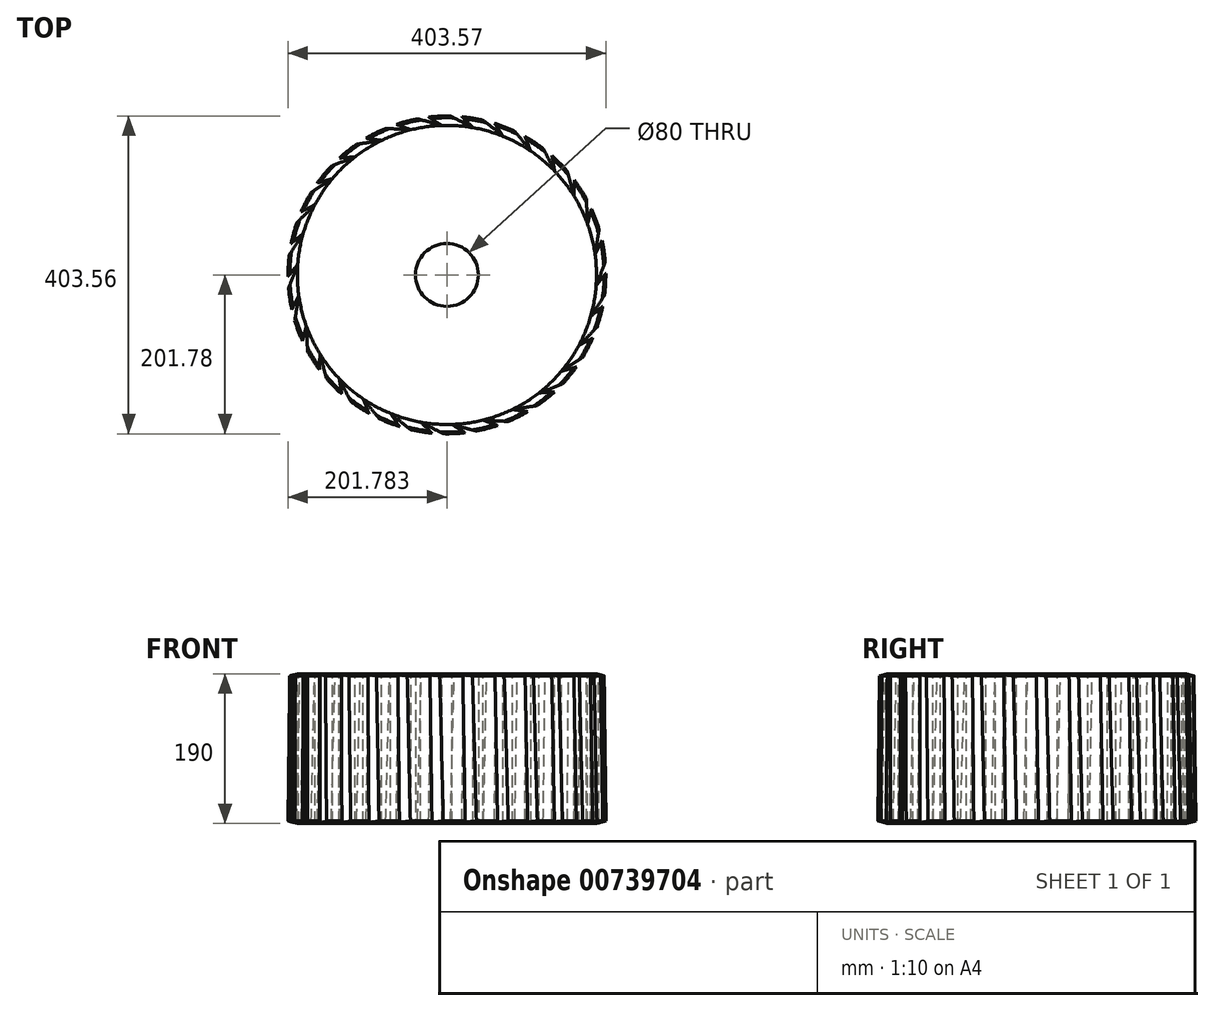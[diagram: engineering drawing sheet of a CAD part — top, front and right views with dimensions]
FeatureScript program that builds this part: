
annotation { "Feature Type Name" : "Feature", "Feature Type Description" : "" }
export const myFeature = defineFeature(function(context is Context, id is Id, definition is map)
    precondition{}
    {
        {
            var Q0;
            Q0=qCreatedBy(makeId("Front.planeOp"),FACE);
            var sketch = newSketch(context, id + "F0", { "sketchPlane" : qUnion([Q0])});
            skLineSegment(sketch, "E0", {"start": v(-135.33, -124.18) * mm, "end": v(-135.33, 192.83) * mm, "construction": true});
            skLineSegment(sketch, "E1.bottom", {"start": v(-325.33, 114.13) * mm, "end": v(-175.33, 114.13) * mm});
            skLineSegment(sketch, "E1.top", {"start": v(-325.33, -75.87) * mm, "end": v(-175.33, -75.87) * mm});
            skLineSegment(sketch, "E1.right", {"start": v(-175.33, 114.13) * mm, "end": v(-175.33, -75.87) * mm});
            skLineSegment(sketch, "E2.right", {"start": v(-334.99, 111.54) * mm, "end": v(-337.11, -72.71) * mm});
            skLineSegment(sketch, "E3", {"start": v(-325.33, 114.13) * mm, "end": v(-334.99, 111.54) * mm});
            skLineSegment(sketch, "E4", {"start": v(-325.33, -75.87) * mm, "end": v(-337.11, -72.71) * mm});
            skSolve(sketch);
        }
        {
            var Q0;
            Q0 = qSketchRegion(id + "F0", true);
            var Q1;
            Q1=sQuery(id+"F0.wireOp",EDGE,"E0");
            revolve(context, id + "F1", {"surfaceOperationType" : NewSurfaceOperationType.NEW, "entities" : qUnion([Q0]), "axis" : qUnion([Q1]), "revolveType" : RevolveType.FULL});
        }
        {
            var Q0;
            Q0=makeQuery(id+"F1.opRevolve","SWEPT_FACE",FACE,{"disambiguationData":[OSD([sQuery(id+"F0.wireOp",EDGE,"E1.bottom")])]});
            var sketch = newSketch(context, id + "F2", { "sketchPlane" : qUnion([Q0])});
            skLineSegment(sketch, "E5", {"start": v(-299.15, 0) * mm, "end": v(273.69, 0) * mm, "construction": true});
            skLineSegment(sketch, "E6", {"start": v(1.56, 131.77) * mm, "end": v(-33.5, 200.96) * mm});
            skLineSegment(sketch, "E7", {"start": v(1.56, 131.77) * mm, "end": v(-10.46, 200.96) * mm});
            skLineSegment(sketch, "E8", {"start": v(-33.5, 200.96) * mm, "end": v(-10.46, 200.96) * mm});
            skPoint(sketch, "E9.end.orphan", {"position": v(-68.57, 270.16) * mm});
            skSolve(sketch);
        }
        {
            var Q0;
            Q0=makeQuery(id+"F2.imprint","IMPRINT",FACE,{"disambiguationData":[TD([[makeQuery(id+"F2.imprint","IMPRINT",EDGE,{"derivedFrom":sQuery(id+"F2.wireOp",EDGE,"E6")}),-1.0]])]});
            extrude(context, id + "F3", {"entities" : qUnion([Q0]), "depth" : 25 * mm, "offsetDistance" : 25 * mm});
        }
        {
            var Q0;
            Q0=makeQuery(id+"F3.opExtrude","CAP_FACE",FACE,{"disambiguationData":[OSD([sQuery(id+"F2.wireOp",EDGE,"E6"),sQuery(id+"F2.wireOp",EDGE,"E7"),sQuery(id+"F2.wireOp",EDGE,"E8")])],"isStart":false});
            extrude(context, id + "F4", {"entities" : qUnion([Q0]), "oppositeDirection" : true, "depth" : 533 * mm, "offsetDistance" : 25 * mm});
        }
        {
            var Q0;
            Q0=makeQuery(id+"F4.opExtrude","SWEPT_BODY",BODY,{"disambiguationData":[OSD([sQuery(id+"F2.wireOp",EDGE,"E6"),sQuery(id+"F2.wireOp",EDGE,"E7"),sQuery(id+"F2.wireOp",EDGE,"E8")])]});
            var Q1;
            Q1=makeQuery(id+"F1.opRevolve","SWEPT_EDGE",EDGE,{"disambiguationData":[OSD([sQuery(id+"F0.wireOp",EDGE,"E1.bottom"),sQuery(id+"F0.wireOp",EDGE,"E1.right")])]});
            circularPattern(context, id + "F5", {"entities" : qUnion([Q0]), "axis" : qUnion([Q1]), "angle" : 360 * degree, "instanceCount" : 30, "equalSpace" : true});
        }
        {
            var Q0;
            Q0=makeQuery(id+"F4.opExtrude","SWEPT_BODY",BODY,{"disambiguationData":[OSD([sQuery(id+"F2.wireOp",EDGE,"E6"),sQuery(id+"F2.wireOp",EDGE,"E7"),sQuery(id+"F2.wireOp",EDGE,"E8")])]});
            var Q1;
            Q1=makeQuery(id+"F5.opPattern","COPY",BODY,{"derivedFrom":makeQuery(id+"F4.opExtrude","SWEPT_BODY",BODY,{"disambiguationData":[OSD([sQuery(id+"F2.wireOp",EDGE,"E6"),sQuery(id+"F2.wireOp",EDGE,"E7"),sQuery(id+"F2.wireOp",EDGE,"E8")])]}),"instanceName":"25"});
            var Q2;
            Q2=makeQuery(id+"F1.opRevolve","SWEPT_BODY",BODY,{"disambiguationData":[OSD([sQuery(id+"F0.wireOp",EDGE,"E1.bottom"),sQuery(id+"F0.wireOp",EDGE,"E1.top"),sQuery(id+"F0.wireOp",EDGE,"E1.right"),sQuery(id+"F0.wireOp",EDGE,"E2.right"),sQuery(id+"F0.wireOp",EDGE,"E3"),sQuery(id+"F0.wireOp",EDGE,"bRj0GN2x-NEWe-g299-EKp4-hdbKCvh0yDdA")])]});
            booleanBodies(context, id + "F6", {"operationType" : BooleanOperationType.SUBTRACTION, "tools" : qUnion([Q0, Q1]), "targets" : qUnion([Q2])});
        }
        {
            var Q0;
            Q0=makeQuery(id+"F3.opExtrude","SWEPT_BODY",BODY,{"disambiguationData":[OSD([sQuery(id+"F2.wireOp",EDGE,"E6"),sQuery(id+"F2.wireOp",EDGE,"E7"),sQuery(id+"F2.wireOp",EDGE,"E8")])]});
            var Q1;
            Q1=makeQuery(id+"F5.opPattern","COPY",BODY,{"derivedFrom":makeQuery(id+"F4.opExtrude","SWEPT_BODY",BODY,{"disambiguationData":[OSD([sQuery(id+"F2.wireOp",EDGE,"E6"),sQuery(id+"F2.wireOp",EDGE,"E7"),sQuery(id+"F2.wireOp",EDGE,"E8")])]}),"instanceName":"1"});
            var Q2;
            Q2=makeQuery(id+"F5.opPattern","COPY",BODY,{"derivedFrom":makeQuery(id+"F4.opExtrude","SWEPT_BODY",BODY,{"disambiguationData":[OSD([sQuery(id+"F2.wireOp",EDGE,"E6"),sQuery(id+"F2.wireOp",EDGE,"E7"),sQuery(id+"F2.wireOp",EDGE,"E8")])]}),"instanceName":"2"});
            var Q3;
            Q3=makeQuery(id+"F1.opRevolve","SWEPT_BODY",BODY,{"disambiguationData":[OSD([sQuery(id+"F0.wireOp",EDGE,"E1.bottom"),sQuery(id+"F0.wireOp",EDGE,"E1.top"),sQuery(id+"F0.wireOp",EDGE,"E1.right"),sQuery(id+"F0.wireOp",EDGE,"E2.right"),sQuery(id+"F0.wireOp",EDGE,"E3"),sQuery(id+"F0.wireOp",EDGE,"bRj0GN2x-NEWe-g299-EKp4-hdbKCvh0yDdA")])]});
            booleanBodies(context, id + "F7", {"operationType" : BooleanOperationType.SUBTRACTION, "tools" : qUnion([Q0, Q1, Q2]), "targets" : qUnion([Q3])});
        }
        {
            var Q0;
            Q0=makeQuery(id+"F5.opPattern","COPY",BODY,{"derivedFrom":makeQuery(id+"F4.opExtrude","SWEPT_BODY",BODY,{"disambiguationData":[OSD([sQuery(id+"F2.wireOp",EDGE,"E6"),sQuery(id+"F2.wireOp",EDGE,"E7"),sQuery(id+"F2.wireOp",EDGE,"E8")])]}),"instanceName":"24"});
            var Q1;
            Q1=makeQuery(id+"F5.opPattern","COPY",BODY,{"derivedFrom":makeQuery(id+"F4.opExtrude","SWEPT_BODY",BODY,{"disambiguationData":[OSD([sQuery(id+"F2.wireOp",EDGE,"E6"),sQuery(id+"F2.wireOp",EDGE,"E7"),sQuery(id+"F2.wireOp",EDGE,"E8")])]}),"instanceName":"23"});
            var Q2;
            Q2=makeQuery(id+"F5.opPattern","COPY",BODY,{"derivedFrom":makeQuery(id+"F4.opExtrude","SWEPT_BODY",BODY,{"disambiguationData":[OSD([sQuery(id+"F2.wireOp",EDGE,"E6"),sQuery(id+"F2.wireOp",EDGE,"E7"),sQuery(id+"F2.wireOp",EDGE,"E8")])]}),"instanceName":"22"});
            var Q3;
            Q3=makeQuery(id+"F5.opPattern","COPY",BODY,{"derivedFrom":makeQuery(id+"F4.opExtrude","SWEPT_BODY",BODY,{"disambiguationData":[OSD([sQuery(id+"F2.wireOp",EDGE,"E6"),sQuery(id+"F2.wireOp",EDGE,"E7"),sQuery(id+"F2.wireOp",EDGE,"E8")])]}),"instanceName":"21"});
            var Q4;
            Q4=makeQuery(id+"F5.opPattern","COPY",BODY,{"derivedFrom":makeQuery(id+"F4.opExtrude","SWEPT_BODY",BODY,{"disambiguationData":[OSD([sQuery(id+"F2.wireOp",EDGE,"E6"),sQuery(id+"F2.wireOp",EDGE,"E7"),sQuery(id+"F2.wireOp",EDGE,"E8")])]}),"instanceName":"20"});
            var Q5;
            Q5=makeQuery(id+"F1.opRevolve","SWEPT_BODY",BODY,{"disambiguationData":[OSD([sQuery(id+"F0.wireOp",EDGE,"E1.bottom"),sQuery(id+"F0.wireOp",EDGE,"E1.top"),sQuery(id+"F0.wireOp",EDGE,"E1.right"),sQuery(id+"F0.wireOp",EDGE,"E2.right"),sQuery(id+"F0.wireOp",EDGE,"E3"),sQuery(id+"F0.wireOp",EDGE,"bRj0GN2x-NEWe-g299-EKp4-hdbKCvh0yDdA")])]});
            booleanBodies(context, id + "F8", {"operationType" : BooleanOperationType.SUBTRACTION, "tools" : qUnion([Q0, Q1, Q2, Q3, Q4]), "targets" : qUnion([Q5])});
        }
        {
            var Q0;
            Q0=makeQuery(id+"F5.opPattern","COPY",BODY,{"derivedFrom":makeQuery(id+"F4.opExtrude","SWEPT_BODY",BODY,{"disambiguationData":[OSD([sQuery(id+"F2.wireOp",EDGE,"E6"),sQuery(id+"F2.wireOp",EDGE,"E7"),sQuery(id+"F2.wireOp",EDGE,"E8")])]}),"instanceName":"15"});
            var Q1;
            Q1=makeQuery(id+"F5.opPattern","COPY",BODY,{"derivedFrom":makeQuery(id+"F4.opExtrude","SWEPT_BODY",BODY,{"disambiguationData":[OSD([sQuery(id+"F2.wireOp",EDGE,"E6"),sQuery(id+"F2.wireOp",EDGE,"E7"),sQuery(id+"F2.wireOp",EDGE,"E8")])]}),"instanceName":"16"});
            var Q2;
            Q2=makeQuery(id+"F5.opPattern","COPY",BODY,{"derivedFrom":makeQuery(id+"F4.opExtrude","SWEPT_BODY",BODY,{"disambiguationData":[OSD([sQuery(id+"F2.wireOp",EDGE,"E6"),sQuery(id+"F2.wireOp",EDGE,"E7"),sQuery(id+"F2.wireOp",EDGE,"E8")])]}),"instanceName":"17"});
            var Q3;
            Q3=makeQuery(id+"F5.opPattern","COPY",BODY,{"derivedFrom":makeQuery(id+"F4.opExtrude","SWEPT_BODY",BODY,{"disambiguationData":[OSD([sQuery(id+"F2.wireOp",EDGE,"E6"),sQuery(id+"F2.wireOp",EDGE,"E7"),sQuery(id+"F2.wireOp",EDGE,"E8")])]}),"instanceName":"18"});
            var Q4;
            Q4=makeQuery(id+"F5.opPattern","COPY",BODY,{"derivedFrom":makeQuery(id+"F4.opExtrude","SWEPT_BODY",BODY,{"disambiguationData":[OSD([sQuery(id+"F2.wireOp",EDGE,"E6"),sQuery(id+"F2.wireOp",EDGE,"E7"),sQuery(id+"F2.wireOp",EDGE,"E8")])]}),"instanceName":"19"});
            var Q5;
            Q5=makeQuery(id+"F1.opRevolve","SWEPT_BODY",BODY,{"disambiguationData":[OSD([sQuery(id+"F0.wireOp",EDGE,"E1.bottom"),sQuery(id+"F0.wireOp",EDGE,"E1.top"),sQuery(id+"F0.wireOp",EDGE,"E1.right"),sQuery(id+"F0.wireOp",EDGE,"E2.right"),sQuery(id+"F0.wireOp",EDGE,"E3"),sQuery(id+"F0.wireOp",EDGE,"bRj0GN2x-NEWe-g299-EKp4-hdbKCvh0yDdA")])]});
            booleanBodies(context, id + "F9", {"operationType" : BooleanOperationType.SUBTRACTION, "tools" : qUnion([Q0, Q1, Q2, Q3, Q4]), "targets" : qUnion([Q5])});
        }
        {
            var Q0;
            Q0=makeQuery(id+"F5.opPattern","COPY",BODY,{"derivedFrom":makeQuery(id+"F4.opExtrude","SWEPT_BODY",BODY,{"disambiguationData":[OSD([sQuery(id+"F2.wireOp",EDGE,"E6"),sQuery(id+"F2.wireOp",EDGE,"E7"),sQuery(id+"F2.wireOp",EDGE,"E8")])]}),"instanceName":"3"});
            var Q1;
            Q1=makeQuery(id+"F5.opPattern","COPY",BODY,{"derivedFrom":makeQuery(id+"F4.opExtrude","SWEPT_BODY",BODY,{"disambiguationData":[OSD([sQuery(id+"F2.wireOp",EDGE,"E6"),sQuery(id+"F2.wireOp",EDGE,"E7"),sQuery(id+"F2.wireOp",EDGE,"E8")])]}),"instanceName":"4"});
            var Q2;
            Q2=makeQuery(id+"F5.opPattern","COPY",BODY,{"derivedFrom":makeQuery(id+"F4.opExtrude","SWEPT_BODY",BODY,{"disambiguationData":[OSD([sQuery(id+"F2.wireOp",EDGE,"E6"),sQuery(id+"F2.wireOp",EDGE,"E7"),sQuery(id+"F2.wireOp",EDGE,"E8")])]}),"instanceName":"5"});
            var Q3;
            Q3=makeQuery(id+"F5.opPattern","COPY",BODY,{"derivedFrom":makeQuery(id+"F4.opExtrude","SWEPT_BODY",BODY,{"disambiguationData":[OSD([sQuery(id+"F2.wireOp",EDGE,"E6"),sQuery(id+"F2.wireOp",EDGE,"E7"),sQuery(id+"F2.wireOp",EDGE,"E8")])]}),"instanceName":"7"});
            var Q4;
            Q4=makeQuery(id+"F5.opPattern","COPY",BODY,{"derivedFrom":makeQuery(id+"F4.opExtrude","SWEPT_BODY",BODY,{"disambiguationData":[OSD([sQuery(id+"F2.wireOp",EDGE,"E6"),sQuery(id+"F2.wireOp",EDGE,"E7"),sQuery(id+"F2.wireOp",EDGE,"E8")])]}),"instanceName":"6"});
            var Q5;
            Q5=makeQuery(id+"F1.opRevolve","SWEPT_BODY",BODY,{"disambiguationData":[OSD([sQuery(id+"F0.wireOp",EDGE,"E1.bottom"),sQuery(id+"F0.wireOp",EDGE,"E1.top"),sQuery(id+"F0.wireOp",EDGE,"E1.right"),sQuery(id+"F0.wireOp",EDGE,"E2.right"),sQuery(id+"F0.wireOp",EDGE,"E3"),sQuery(id+"F0.wireOp",EDGE,"bRj0GN2x-NEWe-g299-EKp4-hdbKCvh0yDdA")])]});
            booleanBodies(context, id + "F10", {"operationType" : BooleanOperationType.SUBTRACTION, "tools" : qUnion([Q0, Q1, Q2, Q3, Q4]), "targets" : qUnion([Q5])});
        }
        {
            var Q0;
            Q0=makeQuery(id+"F5.opPattern","COPY",BODY,{"derivedFrom":makeQuery(id+"F4.opExtrude","SWEPT_BODY",BODY,{"disambiguationData":[OSD([sQuery(id+"F2.wireOp",EDGE,"E6"),sQuery(id+"F2.wireOp",EDGE,"E7"),sQuery(id+"F2.wireOp",EDGE,"E8")])]}),"instanceName":"8"});
            var Q1;
            Q1=makeQuery(id+"F5.opPattern","COPY",BODY,{"derivedFrom":makeQuery(id+"F4.opExtrude","SWEPT_BODY",BODY,{"disambiguationData":[OSD([sQuery(id+"F2.wireOp",EDGE,"E6"),sQuery(id+"F2.wireOp",EDGE,"E7"),sQuery(id+"F2.wireOp",EDGE,"E8")])]}),"instanceName":"9"});
            var Q2;
            Q2=makeQuery(id+"F5.opPattern","COPY",BODY,{"derivedFrom":makeQuery(id+"F4.opExtrude","SWEPT_BODY",BODY,{"disambiguationData":[OSD([sQuery(id+"F2.wireOp",EDGE,"E6"),sQuery(id+"F2.wireOp",EDGE,"E7"),sQuery(id+"F2.wireOp",EDGE,"E8")])]}),"instanceName":"10"});
            var Q3;
            Q3=makeQuery(id+"F5.opPattern","COPY",BODY,{"derivedFrom":makeQuery(id+"F4.opExtrude","SWEPT_BODY",BODY,{"disambiguationData":[OSD([sQuery(id+"F2.wireOp",EDGE,"E6"),sQuery(id+"F2.wireOp",EDGE,"E7"),sQuery(id+"F2.wireOp",EDGE,"E8")])]}),"instanceName":"11"});
            var Q4;
            Q4=makeQuery(id+"F5.opPattern","COPY",BODY,{"derivedFrom":makeQuery(id+"F4.opExtrude","SWEPT_BODY",BODY,{"disambiguationData":[OSD([sQuery(id+"F2.wireOp",EDGE,"E6"),sQuery(id+"F2.wireOp",EDGE,"E7"),sQuery(id+"F2.wireOp",EDGE,"E8")])]}),"instanceName":"12"});
            var Q5;
            Q5=makeQuery(id+"F5.opPattern","COPY",BODY,{"derivedFrom":makeQuery(id+"F4.opExtrude","SWEPT_BODY",BODY,{"disambiguationData":[OSD([sQuery(id+"F2.wireOp",EDGE,"E6"),sQuery(id+"F2.wireOp",EDGE,"E7"),sQuery(id+"F2.wireOp",EDGE,"E8")])]}),"instanceName":"13"});
            var Q6;
            Q6=makeQuery(id+"F5.opPattern","COPY",BODY,{"derivedFrom":makeQuery(id+"F4.opExtrude","SWEPT_BODY",BODY,{"disambiguationData":[OSD([sQuery(id+"F2.wireOp",EDGE,"E6"),sQuery(id+"F2.wireOp",EDGE,"E7"),sQuery(id+"F2.wireOp",EDGE,"E8")])]}),"instanceName":"14"});
            var Q7;
            Q7=makeQuery(id+"F1.opRevolve","SWEPT_BODY",BODY,{"disambiguationData":[OSD([sQuery(id+"F0.wireOp",EDGE,"E1.bottom"),sQuery(id+"F0.wireOp",EDGE,"E1.top"),sQuery(id+"F0.wireOp",EDGE,"E1.right"),sQuery(id+"F0.wireOp",EDGE,"E2.right"),sQuery(id+"F0.wireOp",EDGE,"E3"),sQuery(id+"F0.wireOp",EDGE,"bRj0GN2x-NEWe-g299-EKp4-hdbKCvh0yDdA")])]});
            booleanBodies(context, id + "F11", {"operationType" : BooleanOperationType.SUBTRACTION, "tools" : qUnion([Q0, Q1, Q2, Q3, Q4, Q5, Q6]), "targets" : qUnion([Q7])});
        }
        {
            var Q0;
            Q0=makeQuery(id+"F5.opPattern","COPY",BODY,{"derivedFrom":makeQuery(id+"F4.opExtrude","SWEPT_BODY",BODY,{"disambiguationData":[OSD([sQuery(id+"F2.wireOp",EDGE,"E6"),sQuery(id+"F2.wireOp",EDGE,"E7"),sQuery(id+"F2.wireOp",EDGE,"E8")])]}),"instanceName":"26"});
            var Q1;
            Q1=makeQuery(id+"F5.opPattern","COPY",BODY,{"derivedFrom":makeQuery(id+"F4.opExtrude","SWEPT_BODY",BODY,{"disambiguationData":[OSD([sQuery(id+"F2.wireOp",EDGE,"E6"),sQuery(id+"F2.wireOp",EDGE,"E7"),sQuery(id+"F2.wireOp",EDGE,"E8")])]}),"instanceName":"27"});
            var Q2;
            Q2=makeQuery(id+"F5.opPattern","COPY",BODY,{"derivedFrom":makeQuery(id+"F4.opExtrude","SWEPT_BODY",BODY,{"disambiguationData":[OSD([sQuery(id+"F2.wireOp",EDGE,"E6"),sQuery(id+"F2.wireOp",EDGE,"E7"),sQuery(id+"F2.wireOp",EDGE,"E8")])]}),"instanceName":"28"});
            var Q3;
            Q3=makeQuery(id+"F5.opPattern","COPY",BODY,{"derivedFrom":makeQuery(id+"F4.opExtrude","SWEPT_BODY",BODY,{"disambiguationData":[OSD([sQuery(id+"F2.wireOp",EDGE,"E6"),sQuery(id+"F2.wireOp",EDGE,"E7"),sQuery(id+"F2.wireOp",EDGE,"E8")])]}),"instanceName":"29"});
            var Q4;
            Q4=makeQuery(id+"F1.opRevolve","SWEPT_BODY",BODY,{"disambiguationData":[OSD([sQuery(id+"F0.wireOp",EDGE,"E1.bottom"),sQuery(id+"F0.wireOp",EDGE,"E1.top"),sQuery(id+"F0.wireOp",EDGE,"E1.right"),sQuery(id+"F0.wireOp",EDGE,"E2.right"),sQuery(id+"F0.wireOp",EDGE,"E3"),sQuery(id+"F0.wireOp",EDGE,"E4")])]});
            booleanBodies(context, id + "F12", {"operationType" : BooleanOperationType.SUBTRACTION, "tools" : qUnion([Q0, Q1, Q2, Q3]), "targets" : qUnion([Q4])});
        }
    });
